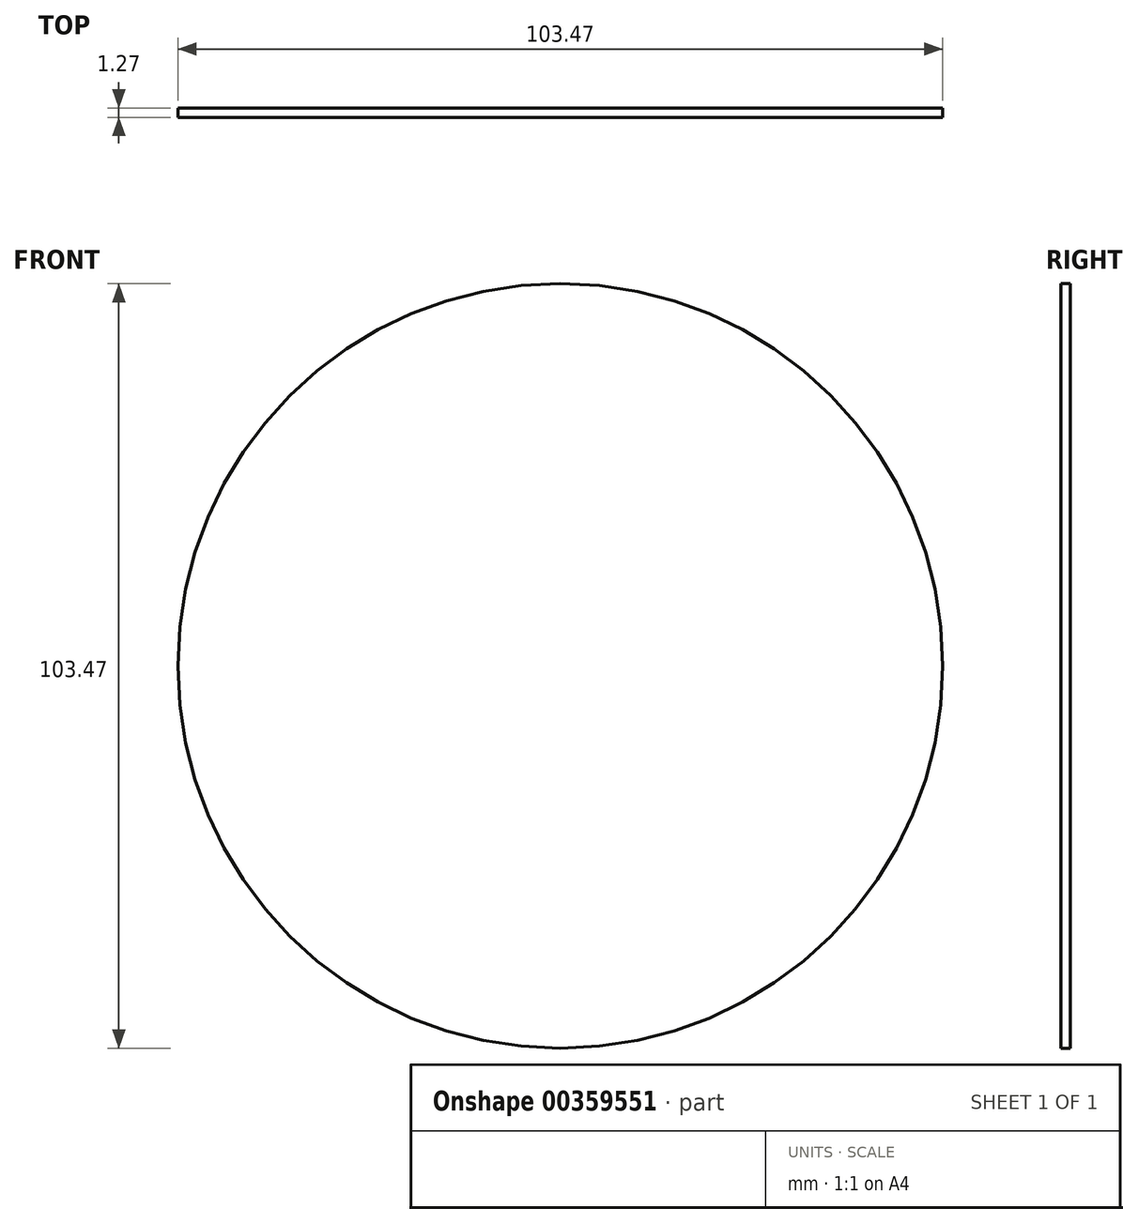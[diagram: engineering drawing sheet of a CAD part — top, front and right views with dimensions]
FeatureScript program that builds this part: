
annotation { "Feature Type Name" : "Feature", "Feature Type Description" : "" }
export const myFeature = defineFeature(function(context is Context, id is Id, definition is map)
    precondition{}
    {
        {
            var Q0;
            Q0=qCreatedBy(makeId("Front.planeOp"),FACE);
            var sketch = newSketch(context, id + "F0", { "sketchPlane" : qUnion([Q0])});
            skCircle(sketch, "E0", {"center": v(-51.06, 23.25) * mm, "radius": 51.73 * mm});
            skSolve(sketch);
        }
        {
            var Q0;
            Q0 = qSketchRegion(id + "F0", true);
            extrude(context, id + "F1", {"entities" : qUnion([Q0]), "depth" : 1.27 * mm});
        }
    });
